# Revit family: 2243
name_source: partatom
category: Plumbing Fixtures
units: mm (PartAtom-declared; Revit-internal decimal feet)

## family parameters
Always vertical = No
Cut with Voids When Loaded = No
OmniClass Number = 23.70.50.21.24
OmniClass Title = Waste Water Drains
Part Type = Normal
Room Calculation Point = No
Round Connector Dimension = Use Diameter
Shared = Yes
Work Plane-Based = Yes

## types (15) — shared parameters
Assembly Code = D2030300
CW Connection = No
Default Elevation = 0"
Description = Deep Body Medium Duty Floor Drains with 12in. Round Tops and Sediment Bucket
Diameter = 15 1/4"
Drain Material = Metal-JayR.Smith-Cast_Iron-Duco_Coated
G - Galvanized Cast Iron = No
HW Connection = No
Installation Type = Floor Mounted
L - Speedi-Set Service Weight - 02"(50), 03"(75) & 04"(100) sizes only = No
LXH - Speedi-Set Extra Heavy - 02"(50), 03"(75) & 04"(100) sizes only = No
Manufacturer = Jay R. Smith
Model = 2240
NB - Nickel Bronze Top = No
Overall Height = 13"
PB - Polished Bronze Top = No
Product Documentation Link = https://www.jrsmith.com
Product Page URL = https://www.jrsmith.com
Quad Close Trap Seal = No
S - Square Top = No
Trap Primer Connection -P050   1/2" (13) & -P075 3/4" (19) = No
U - Vandal Proof Grate = No
URL = http://www.jrsmith.com
Vent Connection = No
Warranty Documentation Link = https://www.jrsmith.com
Waste Connection = Yes

## per-type parameters (varying)
| type | Connection Type | Outlet Diameter | Outlet Radius |
| 2243C02 | Caulk Outlet Connection | 2" | 1" |
| 2243C03 | Caulk Outlet Connection | 3" | 1 1/2" |
| 2243C04 | Caulk Outlet Connection | 4" | 2" |
| 2243C05 | Caulk Outlet Connection | 5" | 2 1/2" |
| 2243C06 | Caulk Outlet Connection | 6" | 3" |
| 2243T02 | Threaded Outlet Connection | 2" | 1" |
| 2243T03 | Threaded Outlet Connection | 3" | 1 1/2" |
| 2243T04 | Threaded Outlet Connection | 4" | 2" |
| 2243T05 | Threaded Outlet Connection | 5" | 2 1/2" |
| 2243T06 | Threaded Outlet Connection | 6" | 3" |
| 2243Y02 | No-HUB Outlet Connection | 2" | 1" |
| 2243Y03 | No-HUB Outlet Connection | 3" | 1 1/2" |
| 2243Y04 | No-HUB Outlet Connection | 4" | 2" |
| 2243Y05 | No-HUB Outlet Connection | 5" | 2 1/2" |
| 2243Y06 | No-HUB Outlet Connection | 6" | 3" |

## geometry (parser evidence)
native form markers: Sweep x2
no freeform markers — native parametric forms only
